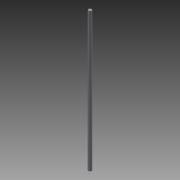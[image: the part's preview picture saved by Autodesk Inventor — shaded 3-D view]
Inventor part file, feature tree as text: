
AUTODESK INVENTOR PART (.ipt)
format: ipt  version: 2013 (Build 170138000, 138)  size: 60,928 bytes
history: native  units: in
note: dims shown in document units (in); Inventor stores cm internally (conversion verified against a paired STEP export)
features: extrude x1, sketch x1
ambient origin geometry x8: Origin, YZ Plane, XZ Plane, XY Plane, X Axis, Y Axis, Z Axis, Center Point
bodies: Solid1 (feature_tree)
feature tree (2):
  extrude  "Extrusion1"  Depth=22.0in TaperAngle=0.0deg
  sketch  "Sketch1"  dims[d0=0.5in d1=22.0in d2=0.0in]
